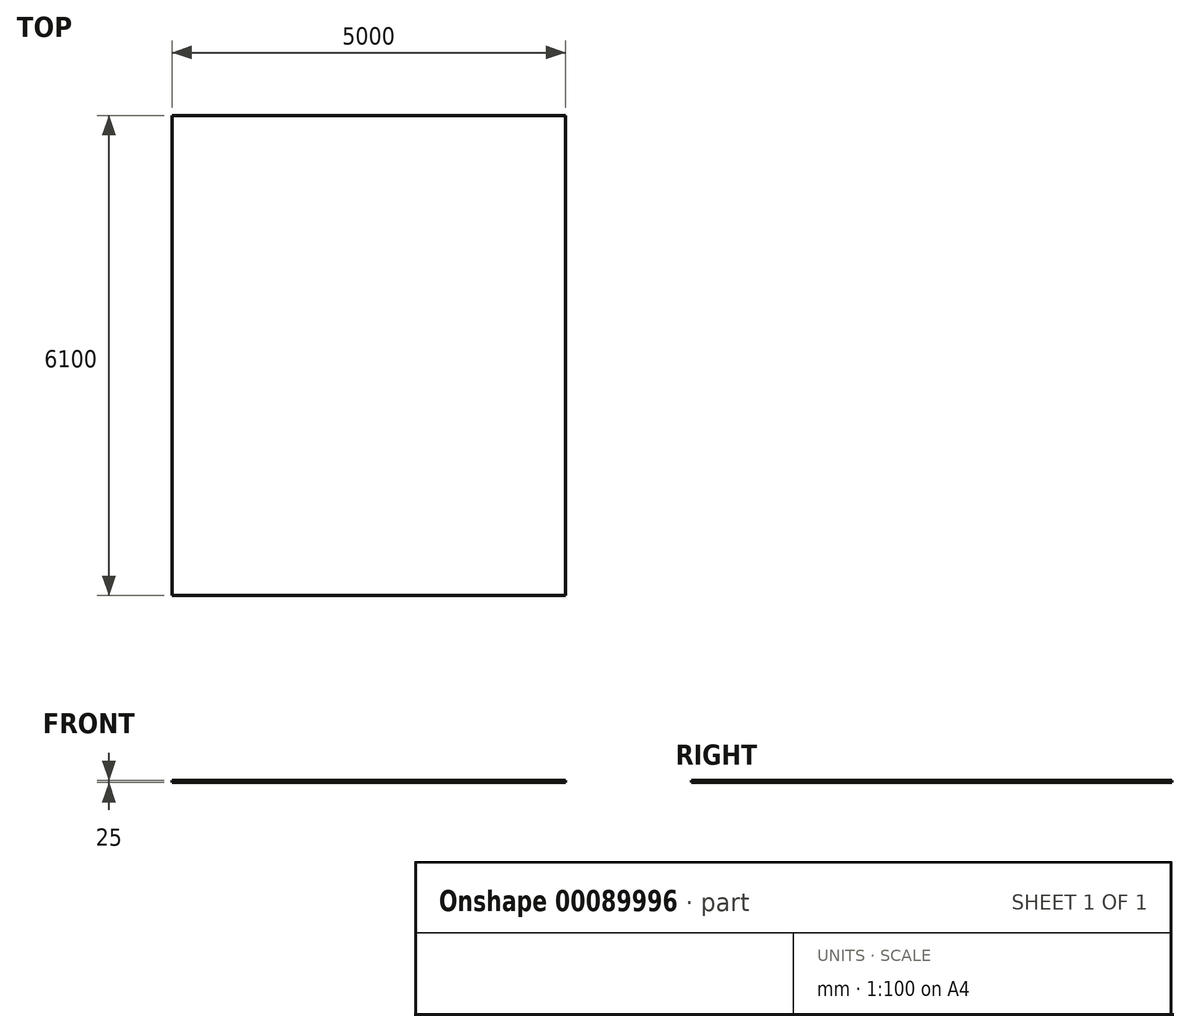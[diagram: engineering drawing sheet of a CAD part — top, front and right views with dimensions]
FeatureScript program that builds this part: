
annotation { "Feature Type Name" : "Feature", "Feature Type Description" : "" }
export const myFeature = defineFeature(function(context is Context, id is Id, definition is map)
    precondition{}
    {
        {
            var Q0;
            Q0=qCreatedBy(makeId("Top.planeOp"),FACE);
            var sketch = newSketch(context, id + "F0", { "sketchPlane" : qUnion([Q0])});
            skLineSegment(sketch, "E0.bottom", {"start": v(0, 0) * mm, "end": v(5000, 0) * mm});
            skLineSegment(sketch, "E0.top", {"start": v(0, 6100) * mm, "end": v(5000, 6100) * mm});
            skLineSegment(sketch, "E0.left", {"start": v(0, 0) * mm, "end": v(0, 6100) * mm});
            skLineSegment(sketch, "E0.right", {"start": v(5000, 0) * mm, "end": v(5000, 6100) * mm});
            skSolve(sketch);
        }
        {
            var Q0;
            Q0 = qSketchRegion(id + "F0", true);
            extrude(context, id + "F1", {"entities" : qUnion([Q0]), "depth" : 25 * mm});
        }
    });
